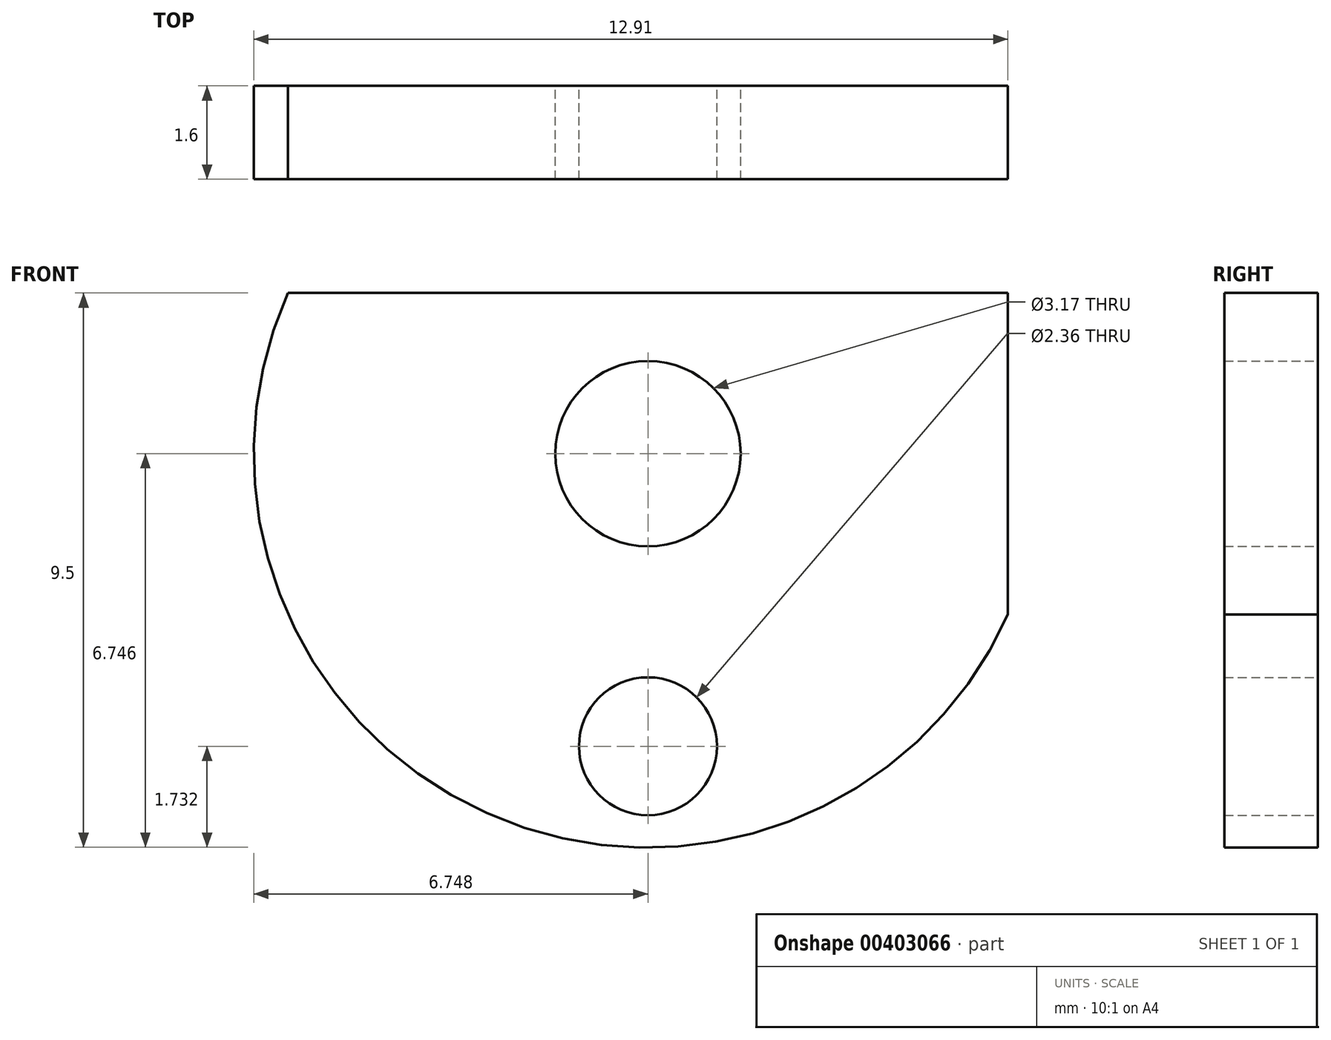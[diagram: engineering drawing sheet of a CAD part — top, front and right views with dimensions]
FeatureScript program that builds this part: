
annotation { "Feature Type Name" : "Feature", "Feature Type Description" : "" }
export const myFeature = defineFeature(function(context is Context, id is Id, definition is map)
    precondition{}
    {
        {
            var Q0;
            Q0=qCreatedBy(makeId("Front.planeOp"),FACE);
            var sketch = newSketch(context, id + "F0", { "sketchPlane" : qUnion([Q0])});
            skArc(sketch, "E0", {"start": v(-7.04, 4) * mm, "mid": v(-3.64, -4.93) * mm, "end": v(5.28, -1.52) * mm});
            skCircle(sketch, "E1", {"center": v(-0.88, 1.24) * mm, "radius": 1.59 * mm});
            skLineSegment(sketch, "E2", {"start": v(-7.04, 4) * mm, "end": v(5.28, 4) * mm});
            skLineSegment(sketch, "E3", {"start": v(5.28, 4) * mm, "end": v(5.28, -1.52) * mm});
            skCircle(sketch, "E4", {"center": v(-0.88, -3.78) * mm, "radius": 1.18 * mm});
            skSolve(sketch);
        }
        {
            var Q0;
            Q0=makeQuery(id+"F0.imprint","IMPRINT",FACE,{"disambiguationData":[TD([[makeQuery(id+"F0.imprint","IMPRINT",EDGE,{"derivedFrom":sQuery(id+"F0.wireOp",EDGE,"E0")}),1.0]])]});
            extrude(context, id + "F1", {"entities" : qUnion([Q0]), "endBound" : BoundingType.SYMMETRIC, "depth" : 1.6 * mm});
        }
    });
